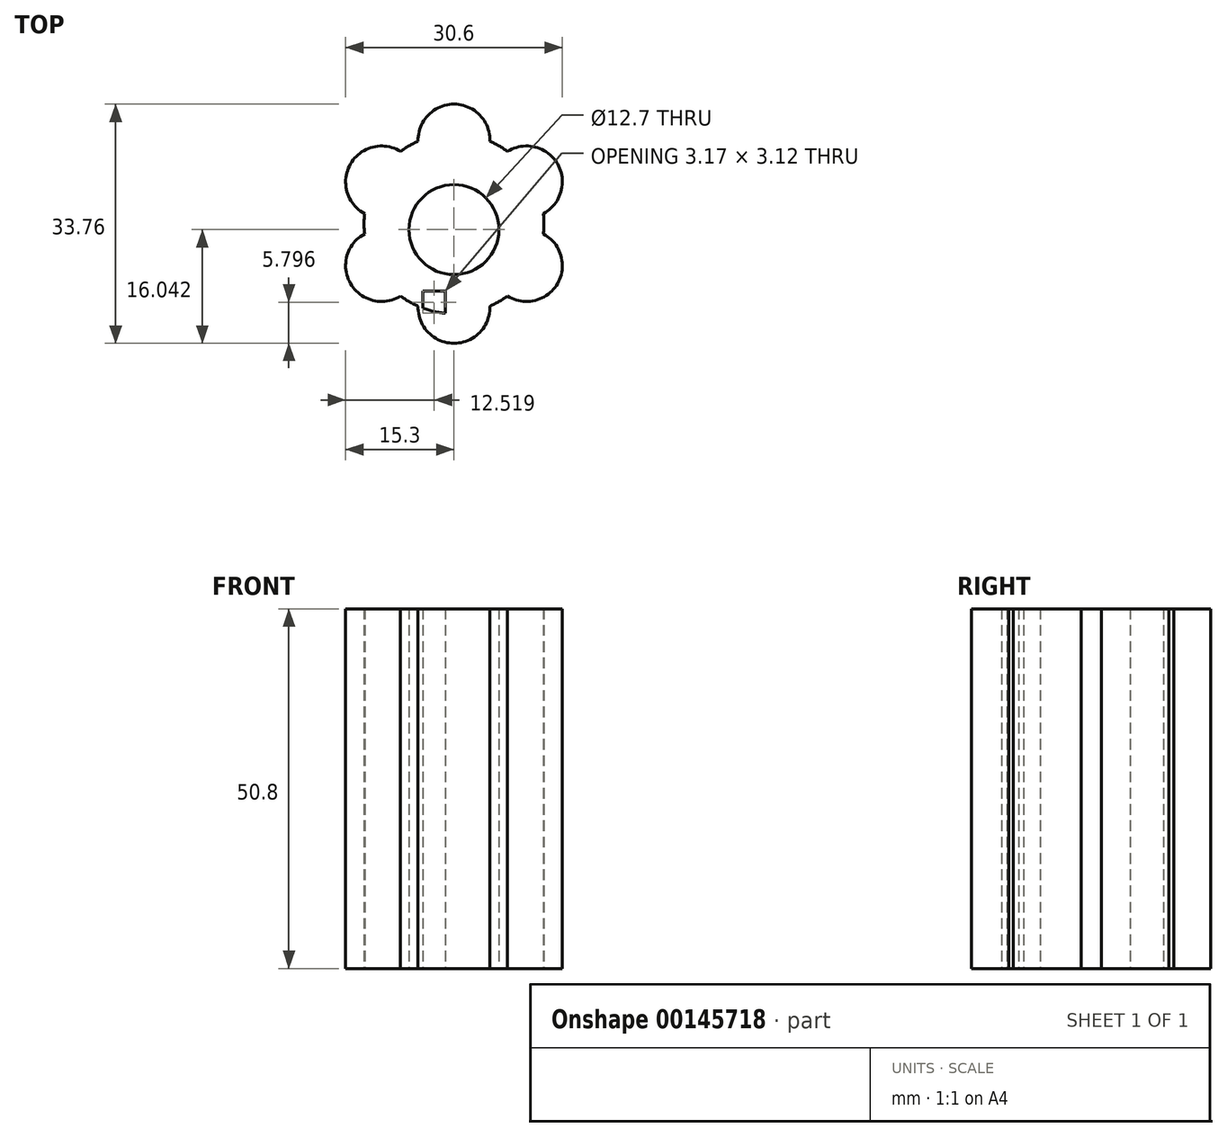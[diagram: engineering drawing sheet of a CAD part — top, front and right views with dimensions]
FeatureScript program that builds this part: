
annotation { "Feature Type Name" : "Feature", "Feature Type Description" : "" }
export const myFeature = defineFeature(function(context is Context, id is Id, definition is map)
    precondition{}
    {
        {
            var Q0;
            Q0=qCreatedBy(makeId("Top.planeOp"),FACE);
            var sketch = newSketch(context, id + "F0", { "sketchPlane" : qUnion([Q0])});
            skCircle(sketch, "E0", {"center": v(0, 0) * mm, "radius": 12.7 * mm, "construction": true});
            skArc(sketch, "E1", {"start": v(0, 16.88) * mm, "mid": v(-3.64, 15.34) * mm, "end": v(-5.07, 11.65) * mm});
            skLineSegment(sketch, "E2", {"start": v(0, 16.88) * mm, "end": v(0, 16.88) * mm});
            skArc(sketch, "E3", {"start": v(5.07, 11.65) * mm, "mid": v(3.64, 15.34) * mm, "end": v(0, 16.88) * mm});
            skLineSegment(sketch, "E4", {"start": v(0, 0) * mm, "end": v(0, 11.81) * mm, "construction": true});
            skArc(sketch, "E5.1.0", {"start": v(-5.07, 11.65) * mm, "mid": v(0, -12.7) * mm, "end": v(5.07, 11.65) * mm, "construction": true});
            skArc(sketch, "E5.1.1", {"start": v(-14.62, -8.44) * mm, "mid": v(-11.46, -10.82) * mm, "end": v(-7.55, -10.21) * mm});
            skArc(sketch, "E5.1.2", {"start": v(-12.62, -1.44) * mm, "mid": v(-15.1, -4.51) * mm, "end": v(-14.62, -8.44) * mm});
            skArc(sketch, "E5.2.0", {"start": v(-7.55, -10.21) * mm, "mid": v(11, -6.35) * mm, "end": v(5.07, 11.65) * mm, "construction": true});
            skArc(sketch, "E5.2.1", {"start": v(14.62, -8.44) * mm, "mid": v(15.1, -4.51) * mm, "end": v(12.62, -1.44) * mm});
            skArc(sketch, "E5.2.2", {"start": v(7.55, -10.21) * mm, "mid": v(11.46, -10.82) * mm, "end": v(14.62, -8.44) * mm});
            skArc(sketch, "E6", {"start": v(-7.55, -10.21) * mm, "mid": v(0, -12.7) * mm, "end": v(7.55, -10.21) * mm});
            skArc(sketch, "E7.trimOffspring", {"start": v(-5.07, 11.65) * mm, "mid": v(-11, 6.35) * mm, "end": v(-12.62, -1.44) * mm});
            skLineSegment(sketch, "E8.trimOffspring", {"start": v(0, 12.7) * mm, "end": v(0, 16.88) * mm, "construction": true});
            skArc(sketch, "E9.trimOffspring", {"start": v(0, 12.7) * mm, "mid": v(-2.59, 12.43) * mm, "end": v(-5.07, 11.65) * mm, "construction": true});
            skArc(sketch, "E10.trimOffspring", {"start": v(12.62, -1.44) * mm, "mid": v(11, 6.35) * mm, "end": v(5.07, 11.65) * mm});
            skCircle(sketch, "E11", {"center": v(0, -0.84) * mm, "radius": 6.35 * mm});
            skLineSegment(sketch, "E12", {"start": v(-4.37, -9.53) * mm, "end": v(-4.37, -11.92) * mm});
            skLineSegment(sketch, "E13", {"start": v(-4.37, -9.53) * mm, "end": v(-1.2, -9.53) * mm});
            skLineSegment(sketch, "E14", {"start": v(-1.2, -12.64) * mm, "end": v(-1.2, -9.53) * mm});
            skLineSegment(sketch, "E15", {"start": v(-2.78, -9.53) * mm, "end": v(0, 0) * mm, "construction": true});
            skArc(sketch, "E16.1.0", {"start": v(-7.55, 10.21) * mm, "mid": v(-11.46, 10.82) * mm, "end": v(-14.62, 8.44) * mm});
            skArc(sketch, "E16.3.0", {"start": v(-5.07, -11.65) * mm, "mid": v(-3.64, -15.34) * mm, "end": v(0, -16.88) * mm});
            skArc(sketch, "E16.5.0", {"start": v(12.62, 1.44) * mm, "mid": v(15.1, 4.51) * mm, "end": v(14.62, 8.44) * mm});
            skArc(sketch, "E17.1.0", {"start": v(14.62, 8.44) * mm, "mid": v(11.46, 10.82) * mm, "end": v(7.55, 10.21) * mm});
            skArc(sketch, "E17.3.0", {"start": v(-14.62, 8.44) * mm, "mid": v(-15.1, 4.51) * mm, "end": v(-12.62, 1.44) * mm});
            skArc(sketch, "E17.5.0", {"start": v(0, -16.88) * mm, "mid": v(3.64, -15.34) * mm, "end": v(5.07, -11.65) * mm});
            skSolve(sketch);
        }
        {
            var Q0;
            Q0 = qSketchRegion(id + "F0", true);
            extrude(context, id + "F1", {"entities" : qUnion([Q0]), "depth" : 50.8 * mm});
        }
    });
